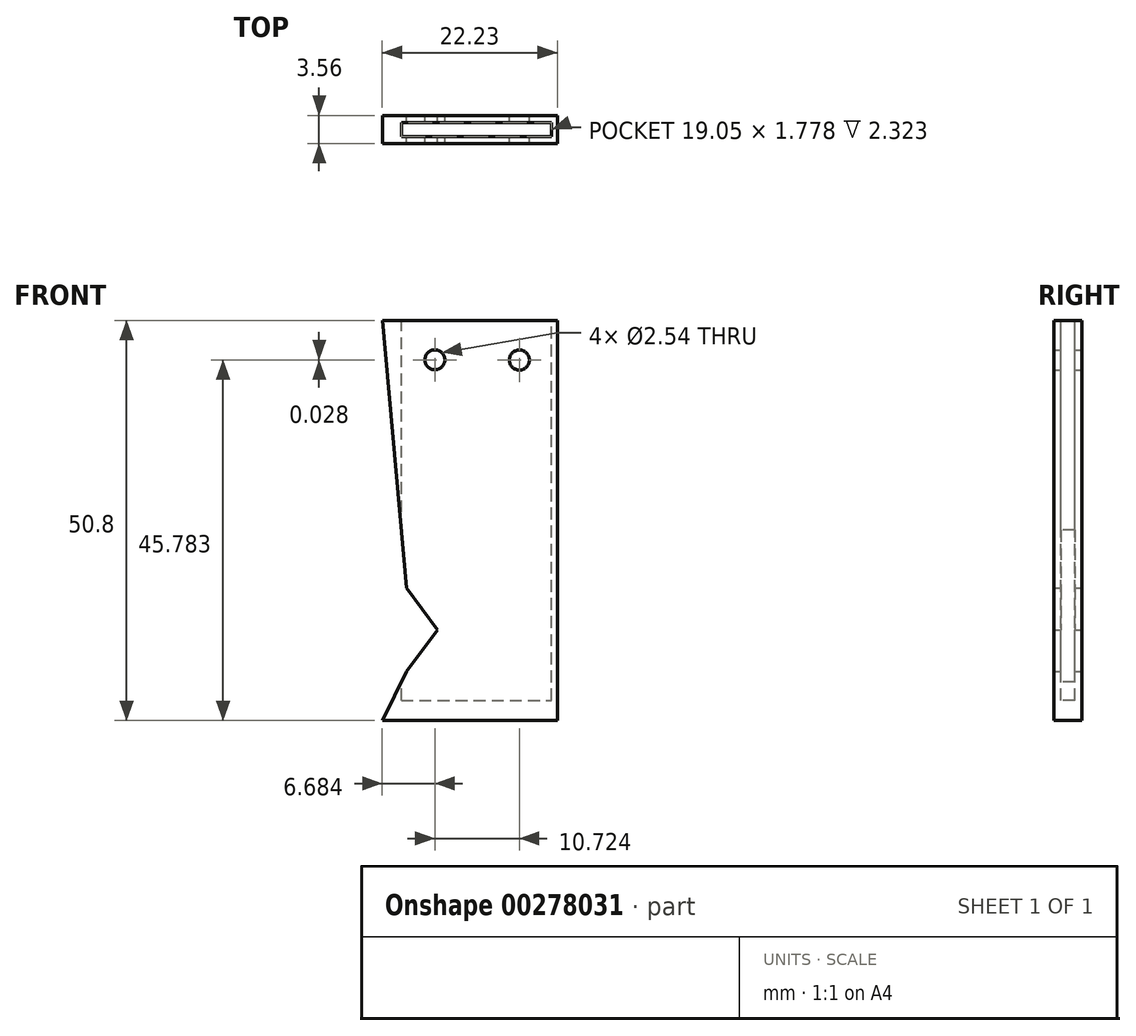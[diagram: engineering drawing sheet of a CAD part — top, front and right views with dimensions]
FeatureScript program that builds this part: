
annotation { "Feature Type Name" : "Feature", "Feature Type Description" : "" }
export const myFeature = defineFeature(function(context is Context, id is Id, definition is map)
    precondition{}
    {
        {
            var Q0;
            Q0=qCreatedBy(makeId("Front.planeOp"),FACE);
            var sketch = newSketch(context, id + "F0", { "sketchPlane" : qUnion([Q0])});
            skLineSegment(sketch, "E0", {"start": v(-43.8, 55.37) * mm, "end": v(-21.58, 55.37) * mm});
            skLineSegment(sketch, "E1", {"start": v(-21.58, 55.37) * mm, "end": v(-21.58, 4.57) * mm});
            skLineSegment(sketch, "E2", {"start": v(-21.58, 4.57) * mm, "end": v(-43.8, 4.57) * mm});
            skCircle(sketch, "E3", {"center": v(-37.13, 50.38) * mm, "radius": 1.27 * mm});
            skCircle(sketch, "E4", {"center": v(-26.4, 50.35) * mm, "radius": 1.27 * mm});
            skLineSegment(sketch, "E5", {"start": v(-43.8, 55.37) * mm, "end": v(-40.73, 21.42) * mm});
            skLineSegment(sketch, "E6", {"start": v(-43.8, 4.57) * mm, "end": v(-40.73, 10.77) * mm});
            skLineSegment(sketch, "E7", {"start": v(-40.73, 10.77) * mm, "end": v(-36.82, 16.1) * mm});
            skLineSegment(sketch, "E8", {"start": v(-40.73, 21.42) * mm, "end": v(-36.82, 16.1) * mm});
            skSolve(sketch);
        }
        {
            var Q0;
            Q0 = qSketchRegion(id + "F0", true);
            extrude(context, id + "F1", {"entities" : qUnion([Q0]), "depth" : 3.56 * mm, "offsetDistance" : 25.4 * mm});
        }
        {
            var Q0;
            Q0=makeQuery(id+"F1.opExtrude","SWEPT_FACE",FACE,{"disambiguationData":[OSD([sQuery(id+"F0.wireOp",EDGE,"E0")])]});
            var sketch = newSketch(context, id + "F2", { "sketchPlane" : qUnion([Q0])});
            skLineSegment(sketch, "E9", {"start": v(-43.8, 0) * mm, "end": v(-43.8, -3.56) * mm});
            skLineSegment(sketch, "E10.bottom", {"start": v(-41.4, -0.89) * mm, "end": v(-22.34, -0.89) * mm});
            skLineSegment(sketch, "E10.top", {"start": v(-41.4, -2.67) * mm, "end": v(-22.34, -2.67) * mm});
            skLineSegment(sketch, "E10.left", {"start": v(-41.4, -0.89) * mm, "end": v(-41.4, -2.67) * mm});
            skLineSegment(sketch, "E10.right", {"start": v(-22.34, -0.89) * mm, "end": v(-22.34, -2.67) * mm});
            skPoint(sketch, "E11.endSnap0", {"position": v(-43.8, -1.78) * mm});
            skLineSegment(sketch, "E12", {"start": v(-34.37, -0.89) * mm, "end": v(-34.37, 0) * mm, "construction": true});
            skLineSegment(sketch, "E13", {"start": v(-34.37, -2.67) * mm, "end": v(-34.37, -3.56) * mm, "construction": true});
            skSolve(sketch);
        }
        {
            var Q0;
            Q0 = qSketchRegion(id + "F2", true);
            extrude(context, id + "F3", {"entities" : qUnion([Q0]), "operationType" : NewBodyOperationType.REMOVE, "oppositeDirection" : true, "depth" : 48.26 * mm});
        }
    });
